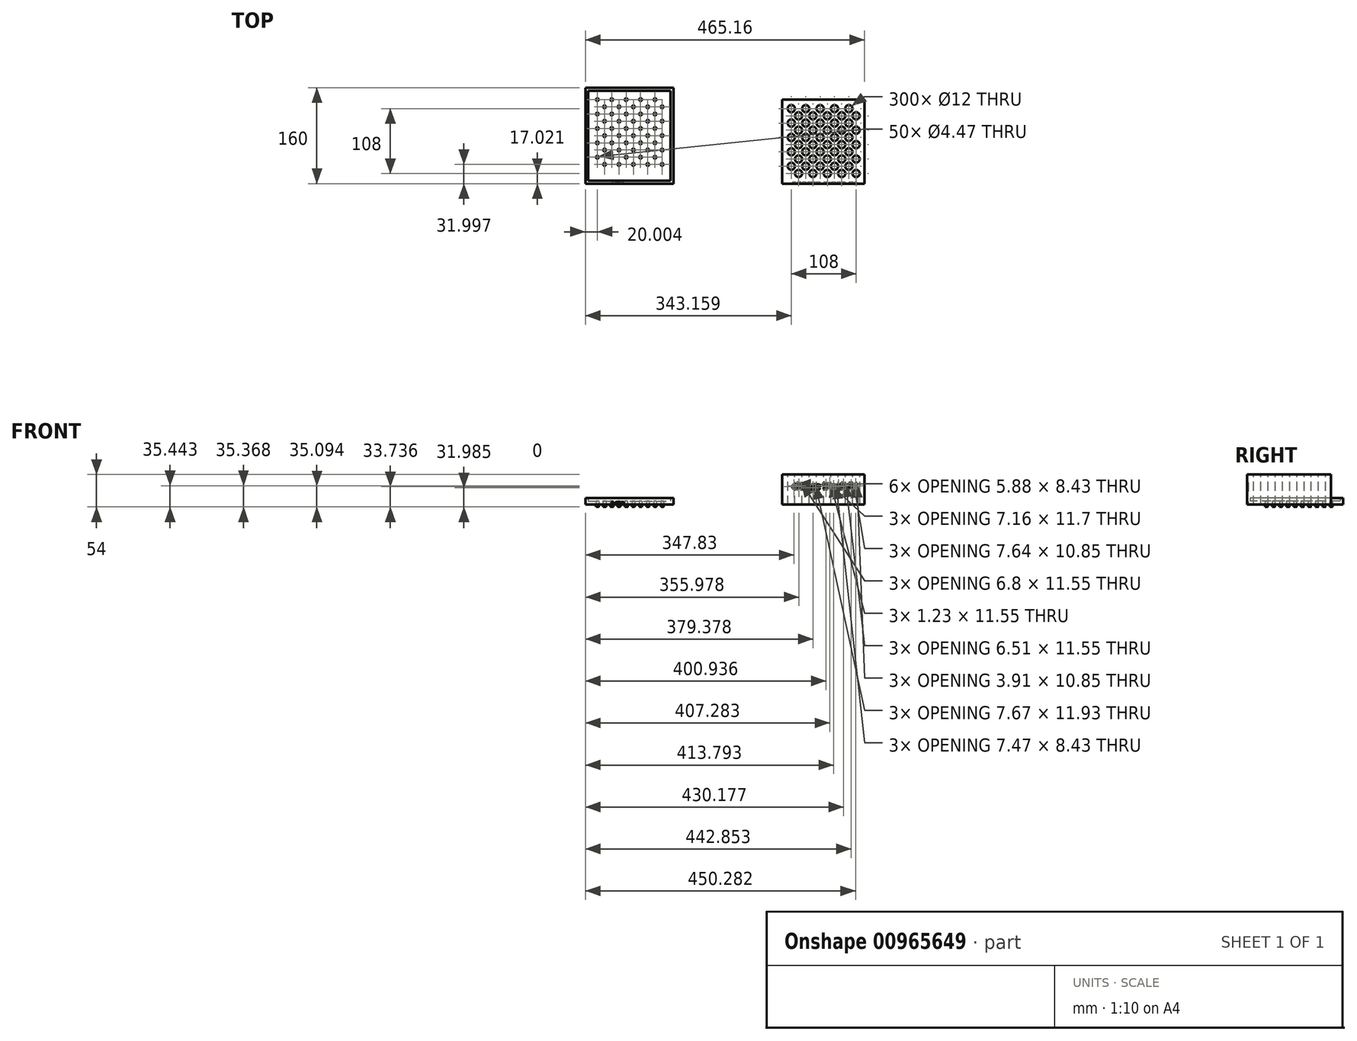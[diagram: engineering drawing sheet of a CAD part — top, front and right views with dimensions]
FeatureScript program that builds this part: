
annotation { "Feature Type Name" : "Feature", "Feature Type Description" : "" }
export const myFeature = defineFeature(function(context is Context, id is Id, definition is map)
    precondition{}
    {
        {
            var Q0;
            Q0=qCreatedBy(makeId("Top.planeOp"),FACE);
            var sketch = newSketch(context, id + "F0", { "sketchPlane" : qUnion([Q0])});
            skLineSegment(sketch, "E0.bottom", {"start": v(-132.2, 107.86) * mm, "end": v(14.8, 107.86) * mm});
            skLineSegment(sketch, "E0.top", {"start": v(-132.2, -52.14) * mm, "end": v(14.8, -52.14) * mm});
            skLineSegment(sketch, "E0.left", {"start": v(-132.2, 107.86) * mm, "end": v(-132.2, -52.14) * mm});
            skLineSegment(sketch, "E0.right", {"start": v(14.8, 107.86) * mm, "end": v(14.8, -52.14) * mm});
            skSolve(sketch);
        }
        {
            var Q0;
            Q0=qSketchRegion(id+"F0",true);
            extrude(context, id + "F1", {"entities" : qUnion([Q0]), "depth" : 6 * mm, "offsetDistance" : 25 * mm});
        }
        {
            var Q0;
            Q0=makeQuery(id+"F1.opExtrude","CAP_FACE",FACE,{"disambiguationData":[OSD([sQuery(id+"F0.wireOp",EDGE,"E0.bottom"),sQuery(id+"F0.wireOp",EDGE,"E0.top"),sQuery(id+"F0.wireOp",EDGE,"E0.left"),sQuery(id+"F0.wireOp",EDGE,"E0.right")])],"isStart":false});
            var sketch = newSketch(context, id + "F2", { "sketchPlane" : qUnion([Q0])});
            skCircle(sketch, "E1", {"center": v(-112.2, 87.86) * mm, "radius": 4 * mm});
            skCircle(sketch, "E2", {"center": v(-100.2, 75.86) * mm, "radius": 4 * mm});
            skCircle(sketch, "E3.0.1.0", {"center": v(-112.2, 63.86) * mm, "radius": 4 * mm});
            skCircle(sketch, "E3.0.1.1", {"center": v(-100.2, 51.86) * mm, "radius": 4 * mm});
            skCircle(sketch, "E3.0.2.0", {"center": v(-112.2, 39.86) * mm, "radius": 4 * mm});
            skCircle(sketch, "E3.0.2.1", {"center": v(-100.2, 27.86) * mm, "radius": 4 * mm});
            skCircle(sketch, "E3.0.3.0", {"center": v(-112.2, 15.86) * mm, "radius": 4 * mm});
            skCircle(sketch, "E3.0.3.1", {"center": v(-100.2, 3.86) * mm, "radius": 4 * mm});
            skCircle(sketch, "E3.0.4.0", {"center": v(-112.2, -8.14) * mm, "radius": 4 * mm});
            skCircle(sketch, "E3.0.4.1", {"center": v(-100.2, -20.14) * mm, "radius": 4 * mm});
            skCircle(sketch, "E3.1.0.0", {"center": v(-88.2, 87.86) * mm, "radius": 4 * mm});
            skCircle(sketch, "E3.1.0.1", {"center": v(-76.2, 75.86) * mm, "radius": 4 * mm});
            skCircle(sketch, "E3.1.1.0", {"center": v(-88.2, 63.86) * mm, "radius": 4 * mm});
            skCircle(sketch, "E3.1.1.1", {"center": v(-76.2, 51.86) * mm, "radius": 4 * mm});
            skCircle(sketch, "E3.1.2.0", {"center": v(-88.2, 39.86) * mm, "radius": 4 * mm});
            skCircle(sketch, "E3.1.2.1", {"center": v(-76.2, 27.86) * mm, "radius": 4 * mm});
            skCircle(sketch, "E3.1.3.0", {"center": v(-88.2, 15.86) * mm, "radius": 4 * mm});
            skCircle(sketch, "E3.1.3.1", {"center": v(-76.2, 3.86) * mm, "radius": 4 * mm});
            skCircle(sketch, "E3.1.4.0", {"center": v(-88.2, -8.14) * mm, "radius": 4 * mm});
            skCircle(sketch, "E3.1.4.1", {"center": v(-76.2, -20.14) * mm, "radius": 4 * mm});
            skCircle(sketch, "E3.2.0.0", {"center": v(-64.2, 87.86) * mm, "radius": 4 * mm});
            skCircle(sketch, "E3.2.0.1", {"center": v(-52.2, 75.86) * mm, "radius": 4 * mm});
            skCircle(sketch, "E3.2.1.0", {"center": v(-64.2, 63.86) * mm, "radius": 4 * mm});
            skCircle(sketch, "E3.2.1.1", {"center": v(-52.2, 51.86) * mm, "radius": 4 * mm});
            skCircle(sketch, "E3.2.2.0", {"center": v(-64.2, 39.86) * mm, "radius": 4 * mm});
            skCircle(sketch, "E3.2.2.1", {"center": v(-52.2, 27.86) * mm, "radius": 4 * mm});
            skCircle(sketch, "E3.2.3.0", {"center": v(-64.2, 15.86) * mm, "radius": 4 * mm});
            skCircle(sketch, "E3.2.3.1", {"center": v(-52.2, 3.86) * mm, "radius": 4 * mm});
            skCircle(sketch, "E3.2.4.0", {"center": v(-64.2, -8.14) * mm, "radius": 4 * mm});
            skCircle(sketch, "E3.2.4.1", {"center": v(-52.2, -20.14) * mm, "radius": 4 * mm});
            skCircle(sketch, "E3.3.0.0", {"center": v(-40.2, 87.86) * mm, "radius": 4 * mm});
            skCircle(sketch, "E3.3.0.1", {"center": v(-28.2, 75.86) * mm, "radius": 4 * mm});
            skCircle(sketch, "E3.3.1.0", {"center": v(-40.2, 63.86) * mm, "radius": 4 * mm});
            skCircle(sketch, "E3.3.1.1", {"center": v(-28.2, 51.86) * mm, "radius": 4 * mm});
            skCircle(sketch, "E3.3.2.0", {"center": v(-40.2, 39.86) * mm, "radius": 4 * mm});
            skCircle(sketch, "E3.3.2.1", {"center": v(-28.2, 27.86) * mm, "radius": 4 * mm});
            skCircle(sketch, "E3.3.3.0", {"center": v(-40.2, 15.86) * mm, "radius": 4 * mm});
            skCircle(sketch, "E3.3.3.1", {"center": v(-28.2, 3.86) * mm, "radius": 4 * mm});
            skCircle(sketch, "E3.3.4.0", {"center": v(-40.2, -8.14) * mm, "radius": 4 * mm});
            skCircle(sketch, "E3.3.4.1", {"center": v(-28.2, -20.14) * mm, "radius": 4 * mm});
            skCircle(sketch, "E3.4.0.0", {"center": v(-16.2, 87.86) * mm, "radius": 4 * mm});
            skCircle(sketch, "E3.4.0.1", {"center": v(-4.2, 75.86) * mm, "radius": 4 * mm});
            skCircle(sketch, "E3.4.1.0", {"center": v(-16.2, 63.86) * mm, "radius": 4 * mm});
            skCircle(sketch, "E3.4.1.1", {"center": v(-4.2, 51.86) * mm, "radius": 4 * mm});
            skCircle(sketch, "E3.4.2.0", {"center": v(-16.2, 39.86) * mm, "radius": 4 * mm});
            skCircle(sketch, "E3.4.2.1", {"center": v(-4.2, 27.86) * mm, "radius": 4 * mm});
            skCircle(sketch, "E3.4.3.0", {"center": v(-16.2, 15.86) * mm, "radius": 4 * mm});
            skCircle(sketch, "E3.4.3.1", {"center": v(-4.2, 3.86) * mm, "radius": 4 * mm});
            skCircle(sketch, "E3.4.4.0", {"center": v(-16.2, -8.14) * mm, "radius": 4 * mm});
            skCircle(sketch, "E3.4.4.1", {"center": v(-4.2, -20.14) * mm, "radius": 4 * mm});
            skLineSegment(sketch, "E3.direction1", {"start": v(-112.2, 87.86) * mm, "end": v(-88.2, 87.86) * mm, "construction": true});
            skLineSegment(sketch, "E3.direction2", {"start": v(-112.2, 87.86) * mm, "end": v(-112.2, 63.86) * mm, "construction": true});
            skSolve(sketch);
        }
        {
            var Q0;
            Q0=makeQuery(id+"F2.imprint","IMPRINT",FACE,{"disambiguationData":[TD([[makeQuery(id+"F2.imprint","IMPRINT",EDGE,{"derivedFrom":sQuery(id+"F2.wireOp",EDGE,"E3.0.1.0")}),1.0]])]});
            var Q1;
            Q1=makeQuery(id+"F2.imprint","IMPRINT",FACE,{"disambiguationData":[TD([[makeQuery(id+"F2.imprint","IMPRINT",EDGE,{"derivedFrom":sQuery(id+"F2.wireOp",EDGE,"E3.1.2.1")}),1.0]])]});
            var Q2;
            Q2=makeQuery(id+"F2.imprint","IMPRINT",FACE,{"disambiguationData":[TD([[makeQuery(id+"F2.imprint","IMPRINT",EDGE,{"derivedFrom":sQuery(id+"F2.wireOp",EDGE,"E3.1.3.0")}),1.0]])]});
            var Q3;
            Q3=makeQuery(id+"F2.imprint","IMPRINT",FACE,{"disambiguationData":[TD([[makeQuery(id+"F2.imprint","IMPRINT",EDGE,{"derivedFrom":sQuery(id+"F2.wireOp",EDGE,"E3.1.4.0")}),1.0]])]});
            var Q4;
            Q4=makeQuery(id+"F2.imprint","IMPRINT",FACE,{"disambiguationData":[TD([[makeQuery(id+"F2.imprint","IMPRINT",EDGE,{"derivedFrom":sQuery(id+"F2.wireOp",EDGE,"E3.2.4.1")}),1.0]])]});
            var Q5;
            Q5=makeQuery(id+"F2.imprint","IMPRINT",FACE,{"disambiguationData":[TD([[makeQuery(id+"F2.imprint","IMPRINT",EDGE,{"derivedFrom":sQuery(id+"F2.wireOp",EDGE,"E3.1.3.1")}),1.0]])]});
            var Q6;
            Q6=makeQuery(id+"F2.imprint","IMPRINT",FACE,{"disambiguationData":[TD([[makeQuery(id+"F2.imprint","IMPRINT",EDGE,{"derivedFrom":sQuery(id+"F2.wireOp",EDGE,"E3.3.0.0")}),1.0]])]});
            var Q7;
            Q7=makeQuery(id+"F2.imprint","IMPRINT",FACE,{"disambiguationData":[TD([[makeQuery(id+"F2.imprint","IMPRINT",EDGE,{"derivedFrom":sQuery(id+"F2.wireOp",EDGE,"E3.3.0.1")}),1.0]])]});
            var Q8;
            Q8=makeQuery(id+"F2.imprint","IMPRINT",FACE,{"disambiguationData":[TD([[makeQuery(id+"F2.imprint","IMPRINT",EDGE,{"derivedFrom":sQuery(id+"F2.wireOp",EDGE,"E3.3.1.0")}),1.0]])]});
            var Q9;
            Q9=makeQuery(id+"F2.imprint","IMPRINT",FACE,{"disambiguationData":[TD([[makeQuery(id+"F2.imprint","IMPRINT",EDGE,{"derivedFrom":sQuery(id+"F2.wireOp",EDGE,"E3.3.1.1")}),1.0]])]});
            var Q10;
            Q10=makeQuery(id+"F2.imprint","IMPRINT",FACE,{"disambiguationData":[TD([[makeQuery(id+"F2.imprint","IMPRINT",EDGE,{"derivedFrom":sQuery(id+"F2.wireOp",EDGE,"E3.3.2.0")}),1.0]])]});
            var Q11;
            Q11=makeQuery(id+"F2.imprint","IMPRINT",FACE,{"disambiguationData":[TD([[makeQuery(id+"F2.imprint","IMPRINT",EDGE,{"derivedFrom":sQuery(id+"F2.wireOp",EDGE,"E3.3.2.1")}),1.0]])]});
            var Q12;
            Q12=makeQuery(id+"F2.imprint","IMPRINT",FACE,{"disambiguationData":[TD([[makeQuery(id+"F2.imprint","IMPRINT",EDGE,{"derivedFrom":sQuery(id+"F2.wireOp",EDGE,"E3.3.3.0")}),1.0]])]});
            var Q13;
            Q13=makeQuery(id+"F2.imprint","IMPRINT",FACE,{"disambiguationData":[TD([[makeQuery(id+"F2.imprint","IMPRINT",EDGE,{"derivedFrom":sQuery(id+"F2.wireOp",EDGE,"E3.3.3.1")}),1.0]])]});
            var Q14;
            Q14=makeQuery(id+"F2.imprint","IMPRINT",FACE,{"disambiguationData":[TD([[makeQuery(id+"F2.imprint","IMPRINT",EDGE,{"derivedFrom":sQuery(id+"F2.wireOp",EDGE,"E3.3.4.0")}),1.0]])]});
            var Q15;
            Q15=makeQuery(id+"F2.imprint","IMPRINT",FACE,{"disambiguationData":[TD([[makeQuery(id+"F2.imprint","IMPRINT",EDGE,{"derivedFrom":sQuery(id+"F2.wireOp",EDGE,"E3.3.4.1")}),1.0]])]});
            var Q16;
            Q16=makeQuery(id+"F2.imprint","IMPRINT",FACE,{"disambiguationData":[TD([[makeQuery(id+"F2.imprint","IMPRINT",EDGE,{"derivedFrom":sQuery(id+"F2.wireOp",EDGE,"E3.4.0.0")}),1.0]])]});
            var Q17;
            Q17=makeQuery(id+"F2.imprint","IMPRINT",FACE,{"disambiguationData":[TD([[makeQuery(id+"F2.imprint","IMPRINT",EDGE,{"derivedFrom":sQuery(id+"F2.wireOp",EDGE,"E3.4.3.1")}),1.0]])]});
            var Q18;
            Q18=makeQuery(id+"F2.imprint","IMPRINT",FACE,{"disambiguationData":[TD([[makeQuery(id+"F2.imprint","IMPRINT",EDGE,{"derivedFrom":sQuery(id+"F2.wireOp",EDGE,"E1")}),1.0]])]});
            var Q19;
            Q19=makeQuery(id+"F2.imprint","IMPRINT",FACE,{"disambiguationData":[TD([[makeQuery(id+"F2.imprint","IMPRINT",EDGE,{"derivedFrom":sQuery(id+"F2.wireOp",EDGE,"E3.4.4.0")}),1.0]])]});
            var Q20;
            Q20=makeQuery(id+"F2.imprint","IMPRINT",FACE,{"disambiguationData":[TD([[makeQuery(id+"F2.imprint","IMPRINT",EDGE,{"derivedFrom":sQuery(id+"F2.wireOp",EDGE,"E2")}),1.0]])]});
            var Q21;
            Q21=makeQuery(id+"F2.imprint","IMPRINT",FACE,{"disambiguationData":[TD([[makeQuery(id+"F2.imprint","IMPRINT",EDGE,{"derivedFrom":sQuery(id+"F2.wireOp",EDGE,"E3.4.4.1")}),1.0]])]});
            var Q22;
            Q22=makeQuery(id+"F2.imprint","IMPRINT",FACE,{"disambiguationData":[TD([[makeQuery(id+"F2.imprint","IMPRINT",EDGE,{"derivedFrom":sQuery(id+"F2.wireOp",EDGE,"E3.0.1.1")}),1.0]])]});
            var Q23;
            Q23=makeQuery(id+"F2.imprint","IMPRINT",FACE,{"disambiguationData":[TD([[makeQuery(id+"F2.imprint","IMPRINT",EDGE,{"derivedFrom":sQuery(id+"F2.wireOp",EDGE,"E3.4.3.0")}),1.0]])]});
            var Q24;
            Q24=makeQuery(id+"F2.imprint","IMPRINT",FACE,{"disambiguationData":[TD([[makeQuery(id+"F2.imprint","IMPRINT",EDGE,{"derivedFrom":sQuery(id+"F2.wireOp",EDGE,"E3.4.2.1")}),1.0]])]});
            var Q25;
            Q25=makeQuery(id+"F2.imprint","IMPRINT",FACE,{"disambiguationData":[TD([[makeQuery(id+"F2.imprint","IMPRINT",EDGE,{"derivedFrom":sQuery(id+"F2.wireOp",EDGE,"E3.4.2.0")}),1.0]])]});
            var Q26;
            Q26=makeQuery(id+"F2.imprint","IMPRINT",FACE,{"disambiguationData":[TD([[makeQuery(id+"F2.imprint","IMPRINT",EDGE,{"derivedFrom":sQuery(id+"F2.wireOp",EDGE,"E3.4.1.1")}),1.0]])]});
            var Q27;
            Q27=makeQuery(id+"F2.imprint","IMPRINT",FACE,{"disambiguationData":[TD([[makeQuery(id+"F2.imprint","IMPRINT",EDGE,{"derivedFrom":sQuery(id+"F2.wireOp",EDGE,"E3.4.1.0")}),1.0]])]});
            var Q28;
            Q28=makeQuery(id+"F2.imprint","IMPRINT",FACE,{"disambiguationData":[TD([[makeQuery(id+"F2.imprint","IMPRINT",EDGE,{"derivedFrom":sQuery(id+"F2.wireOp",EDGE,"E3.4.0.1")}),1.0]])]});
            var Q29;
            Q29=makeQuery(id+"F2.imprint","IMPRINT",FACE,{"disambiguationData":[TD([[makeQuery(id+"F2.imprint","IMPRINT",EDGE,{"derivedFrom":sQuery(id+"F2.wireOp",EDGE,"E3.2.4.0")}),1.0]])]});
            var Q30;
            Q30=makeQuery(id+"F2.imprint","IMPRINT",FACE,{"disambiguationData":[TD([[makeQuery(id+"F2.imprint","IMPRINT",EDGE,{"derivedFrom":sQuery(id+"F2.wireOp",EDGE,"E3.2.3.1")}),1.0]])]});
            var Q31;
            Q31=makeQuery(id+"F2.imprint","IMPRINT",FACE,{"disambiguationData":[TD([[makeQuery(id+"F2.imprint","IMPRINT",EDGE,{"derivedFrom":sQuery(id+"F2.wireOp",EDGE,"E3.2.3.0")}),1.0]])]});
            var Q32;
            Q32=makeQuery(id+"F2.imprint","IMPRINT",FACE,{"disambiguationData":[TD([[makeQuery(id+"F2.imprint","IMPRINT",EDGE,{"derivedFrom":sQuery(id+"F2.wireOp",EDGE,"E3.2.2.1")}),1.0]])]});
            var Q33;
            Q33=makeQuery(id+"F2.imprint","IMPRINT",FACE,{"disambiguationData":[TD([[makeQuery(id+"F2.imprint","IMPRINT",EDGE,{"derivedFrom":sQuery(id+"F2.wireOp",EDGE,"E3.2.2.0")}),1.0]])]});
            var Q34;
            Q34=makeQuery(id+"F2.imprint","IMPRINT",FACE,{"disambiguationData":[TD([[makeQuery(id+"F2.imprint","IMPRINT",EDGE,{"derivedFrom":sQuery(id+"F2.wireOp",EDGE,"E3.2.1.1")}),1.0]])]});
            var Q35;
            Q35=makeQuery(id+"F2.imprint","IMPRINT",FACE,{"disambiguationData":[TD([[makeQuery(id+"F2.imprint","IMPRINT",EDGE,{"derivedFrom":sQuery(id+"F2.wireOp",EDGE,"E3.2.1.0")}),1.0]])]});
            var Q36;
            Q36=makeQuery(id+"F2.imprint","IMPRINT",FACE,{"disambiguationData":[TD([[makeQuery(id+"F2.imprint","IMPRINT",EDGE,{"derivedFrom":sQuery(id+"F2.wireOp",EDGE,"E3.2.0.1")}),1.0]])]});
            var Q37;
            Q37=makeQuery(id+"F2.imprint","IMPRINT",FACE,{"disambiguationData":[TD([[makeQuery(id+"F2.imprint","IMPRINT",EDGE,{"derivedFrom":sQuery(id+"F2.wireOp",EDGE,"E3.2.0.0")}),1.0]])]});
            var Q38;
            Q38=makeQuery(id+"F2.imprint","IMPRINT",FACE,{"disambiguationData":[TD([[makeQuery(id+"F2.imprint","IMPRINT",EDGE,{"derivedFrom":sQuery(id+"F2.wireOp",EDGE,"E3.1.4.1")}),1.0]])]});
            var Q39;
            Q39=makeQuery(id+"F2.imprint","IMPRINT",FACE,{"disambiguationData":[TD([[makeQuery(id+"F2.imprint","IMPRINT",EDGE,{"derivedFrom":sQuery(id+"F2.wireOp",EDGE,"E3.1.2.0")}),1.0]])]});
            var Q40;
            Q40=makeQuery(id+"F2.imprint","IMPRINT",FACE,{"disambiguationData":[TD([[makeQuery(id+"F2.imprint","IMPRINT",EDGE,{"derivedFrom":sQuery(id+"F2.wireOp",EDGE,"E3.1.1.1")}),1.0]])]});
            var Q41;
            Q41=makeQuery(id+"F2.imprint","IMPRINT",FACE,{"disambiguationData":[TD([[makeQuery(id+"F2.imprint","IMPRINT",EDGE,{"derivedFrom":sQuery(id+"F2.wireOp",EDGE,"E3.1.1.0")}),1.0]])]});
            var Q42;
            Q42=makeQuery(id+"F2.imprint","IMPRINT",FACE,{"disambiguationData":[TD([[makeQuery(id+"F2.imprint","IMPRINT",EDGE,{"derivedFrom":sQuery(id+"F2.wireOp",EDGE,"E3.1.0.1")}),1.0]])]});
            var Q43;
            Q43=makeQuery(id+"F2.imprint","IMPRINT",FACE,{"disambiguationData":[TD([[makeQuery(id+"F2.imprint","IMPRINT",EDGE,{"derivedFrom":sQuery(id+"F2.wireOp",EDGE,"E3.1.0.0")}),1.0]])]});
            var Q44;
            Q44=makeQuery(id+"F2.imprint","IMPRINT",FACE,{"disambiguationData":[TD([[makeQuery(id+"F2.imprint","IMPRINT",EDGE,{"derivedFrom":sQuery(id+"F2.wireOp",EDGE,"E3.0.4.1")}),1.0]])]});
            var Q45;
            Q45=makeQuery(id+"F2.imprint","IMPRINT",FACE,{"disambiguationData":[TD([[makeQuery(id+"F2.imprint","IMPRINT",EDGE,{"derivedFrom":sQuery(id+"F2.wireOp",EDGE,"E3.0.4.0")}),1.0]])]});
            var Q46;
            Q46=makeQuery(id+"F2.imprint","IMPRINT",FACE,{"disambiguationData":[TD([[makeQuery(id+"F2.imprint","IMPRINT",EDGE,{"derivedFrom":sQuery(id+"F2.wireOp",EDGE,"E3.0.3.1")}),1.0]])]});
            var Q47;
            Q47=makeQuery(id+"F2.imprint","IMPRINT",FACE,{"disambiguationData":[TD([[makeQuery(id+"F2.imprint","IMPRINT",EDGE,{"derivedFrom":sQuery(id+"F2.wireOp",EDGE,"E3.0.3.0")}),1.0]])]});
            var Q48;
            Q48=makeQuery(id+"F2.imprint","IMPRINT",FACE,{"disambiguationData":[TD([[makeQuery(id+"F2.imprint","IMPRINT",EDGE,{"derivedFrom":sQuery(id+"F2.wireOp",EDGE,"E3.0.2.1")}),1.0]])]});
            var Q49;
            Q49=makeQuery(id+"F2.imprint","IMPRINT",FACE,{"disambiguationData":[TD([[makeQuery(id+"F2.imprint","IMPRINT",EDGE,{"derivedFrom":sQuery(id+"F2.wireOp",EDGE,"E3.0.2.0")}),1.0]])]});
            extrude(context, id + "F3", {"entities" : qUnion([Q0, Q1, Q2, Q3, Q4, Q5, Q6, Q7, Q8, Q9, Q10, Q11, Q12, Q13, Q14, Q15, Q16, Q17, Q18, Q19, Q20, Q21, Q22, Q23, Q24, Q25, Q26, Q27, Q28, Q29, Q30, Q31, Q32, Q33, Q34, Q35, Q36, Q37, Q38, Q39, Q40, Q41, Q42, Q43, Q44, Q45, Q46, Q47, Q48, Q49]), "operationType" : NewBodyOperationType.ADD, "oppositeDirection" : true, "depth" : 10 * mm, "offsetDistance" : 25 * mm, "hasDraft" : true, "draftAngle" : 10 * degree, "draftPullDirection" : true});
        }
        {
            var Q0;
            Q0=makeQuery(id+"F1.opExtrude","CAP_FACE",FACE,{"disambiguationData":[OSD([sQuery(id+"F0.wireOp",EDGE,"E0.bottom"),sQuery(id+"F0.wireOp",EDGE,"E0.top"),sQuery(id+"F0.wireOp",EDGE,"E0.left"),sQuery(id+"F0.wireOp",EDGE,"E0.right")])],"isStart":false});
            var sketch = newSketch(context, id + "F4", { "sketchPlane" : qUnion([Q0])});
            skCircle(sketch, "E4", {"center": v(-112.2, 87.86) * mm, "radius": 1.75 * mm});
            skCircle(sketch, "E5", {"center": v(-100.2, 75.86) * mm, "radius": 1.75 * mm});
            skCircle(sketch, "E6.0.1.0", {"center": v(-112.2, 63.86) * mm, "radius": 1.75 * mm});
            skCircle(sketch, "E6.0.1.1", {"center": v(-100.2, 51.86) * mm, "radius": 1.75 * mm});
            skCircle(sketch, "E6.0.2.0", {"center": v(-112.2, 39.86) * mm, "radius": 1.75 * mm});
            skCircle(sketch, "E6.0.2.1", {"center": v(-100.2, 27.86) * mm, "radius": 1.75 * mm});
            skCircle(sketch, "E6.0.3.0", {"center": v(-112.2, 15.86) * mm, "radius": 1.75 * mm});
            skCircle(sketch, "E6.0.3.1", {"center": v(-100.2, 3.86) * mm, "radius": 1.75 * mm});
            skCircle(sketch, "E6.0.4.0", {"center": v(-112.2, -8.14) * mm, "radius": 1.75 * mm});
            skCircle(sketch, "E6.0.4.1", {"center": v(-100.2, -20.14) * mm, "radius": 1.75 * mm});
            skCircle(sketch, "E6.1.0.0", {"center": v(-88.2, 87.86) * mm, "radius": 1.75 * mm});
            skCircle(sketch, "E6.1.0.1", {"center": v(-76.2, 75.86) * mm, "radius": 1.75 * mm});
            skCircle(sketch, "E6.1.1.0", {"center": v(-88.2, 63.86) * mm, "radius": 1.75 * mm});
            skCircle(sketch, "E6.1.1.1", {"center": v(-76.2, 51.86) * mm, "radius": 1.75 * mm});
            skCircle(sketch, "E6.1.2.0", {"center": v(-88.2, 39.86) * mm, "radius": 1.75 * mm});
            skCircle(sketch, "E6.1.2.1", {"center": v(-76.2, 27.86) * mm, "radius": 1.75 * mm});
            skCircle(sketch, "E6.1.3.0", {"center": v(-88.2, 15.86) * mm, "radius": 1.75 * mm});
            skCircle(sketch, "E6.1.3.1", {"center": v(-76.2, 3.86) * mm, "radius": 1.75 * mm});
            skCircle(sketch, "E6.1.4.0", {"center": v(-88.2, -8.14) * mm, "radius": 1.75 * mm});
            skCircle(sketch, "E6.1.4.1", {"center": v(-76.2, -20.14) * mm, "radius": 1.75 * mm});
            skCircle(sketch, "E6.2.0.0", {"center": v(-64.2, 87.86) * mm, "radius": 1.75 * mm});
            skCircle(sketch, "E6.2.0.1", {"center": v(-52.2, 75.86) * mm, "radius": 1.75 * mm});
            skCircle(sketch, "E6.2.1.0", {"center": v(-64.2, 63.86) * mm, "radius": 1.75 * mm});
            skCircle(sketch, "E6.2.1.1", {"center": v(-52.2, 51.86) * mm, "radius": 1.75 * mm});
            skCircle(sketch, "E6.2.2.0", {"center": v(-64.2, 39.86) * mm, "radius": 1.75 * mm});
            skCircle(sketch, "E6.2.2.1", {"center": v(-52.2, 27.86) * mm, "radius": 1.75 * mm});
            skCircle(sketch, "E6.2.3.0", {"center": v(-64.2, 15.86) * mm, "radius": 1.75 * mm});
            skCircle(sketch, "E6.2.3.1", {"center": v(-52.2, 3.86) * mm, "radius": 1.75 * mm});
            skCircle(sketch, "E6.2.4.0", {"center": v(-64.2, -8.14) * mm, "radius": 1.75 * mm});
            skCircle(sketch, "E6.2.4.1", {"center": v(-52.2, -20.14) * mm, "radius": 1.75 * mm});
            skCircle(sketch, "E6.3.0.0", {"center": v(-40.2, 87.86) * mm, "radius": 1.75 * mm});
            skCircle(sketch, "E6.3.0.1", {"center": v(-28.2, 75.86) * mm, "radius": 1.75 * mm});
            skCircle(sketch, "E6.3.1.0", {"center": v(-40.2, 63.86) * mm, "radius": 1.75 * mm});
            skCircle(sketch, "E6.3.1.1", {"center": v(-28.2, 51.86) * mm, "radius": 1.75 * mm});
            skCircle(sketch, "E6.3.2.0", {"center": v(-40.2, 39.86) * mm, "radius": 1.75 * mm});
            skCircle(sketch, "E6.3.2.1", {"center": v(-28.2, 27.86) * mm, "radius": 1.75 * mm});
            skCircle(sketch, "E6.3.3.0", {"center": v(-40.2, 15.86) * mm, "radius": 1.75 * mm});
            skCircle(sketch, "E6.3.3.1", {"center": v(-28.2, 3.86) * mm, "radius": 1.75 * mm});
            skCircle(sketch, "E6.3.4.0", {"center": v(-40.2, -8.14) * mm, "radius": 1.75 * mm});
            skCircle(sketch, "E6.3.4.1", {"center": v(-28.2, -20.14) * mm, "radius": 1.75 * mm});
            skCircle(sketch, "E6.4.0.0", {"center": v(-16.2, 87.86) * mm, "radius": 1.75 * mm});
            skCircle(sketch, "E6.4.0.1", {"center": v(-4.2, 75.86) * mm, "radius": 1.75 * mm});
            skCircle(sketch, "E6.4.1.0", {"center": v(-16.2, 63.86) * mm, "radius": 1.75 * mm});
            skCircle(sketch, "E6.4.1.1", {"center": v(-4.2, 51.86) * mm, "radius": 1.75 * mm});
            skCircle(sketch, "E6.4.2.0", {"center": v(-16.2, 39.86) * mm, "radius": 1.75 * mm});
            skCircle(sketch, "E6.4.2.1", {"center": v(-4.2, 27.86) * mm, "radius": 1.75 * mm});
            skCircle(sketch, "E6.4.3.0", {"center": v(-16.2, 15.86) * mm, "radius": 1.75 * mm});
            skCircle(sketch, "E6.4.3.1", {"center": v(-4.2, 3.86) * mm, "radius": 1.75 * mm});
            skCircle(sketch, "E6.4.4.0", {"center": v(-16.2, -8.14) * mm, "radius": 1.75 * mm});
            skCircle(sketch, "E6.4.4.1", {"center": v(-4.2, -20.14) * mm, "radius": 1.75 * mm});
            skLineSegment(sketch, "E6.direction1", {"start": v(-112.2, 87.86) * mm, "end": v(-88.2, 87.86) * mm, "construction": true});
            skLineSegment(sketch, "E6.direction2", {"start": v(-112.2, 87.86) * mm, "end": v(-112.2, 63.86) * mm, "construction": true});
            skSolve(sketch);
        }
        {
            var Q0;
            Q0=makeQuery(id+"F3.opExtrude","CAP_FACE",FACE,{"disambiguationData":[OSD([sQuery(id+"F2.wireOp",EDGE,"E3.1.4.1")])],"isStart":false});
            var Q1;
            Q1=makeQuery(id+"F3.opExtrude","CAP_FACE",FACE,{"disambiguationData":[OSD([sQuery(id+"F2.wireOp",EDGE,"E3.4.0.1")])],"isStart":false});
            var Q2;
            Q2=makeQuery(id+"F3.opExtrude","CAP_FACE",FACE,{"disambiguationData":[OSD([sQuery(id+"F2.wireOp",EDGE,"E3.3.0.0")])],"isStart":false});
            var Q3;
            Q3=makeQuery(id+"F3.opExtrude","CAP_FACE",FACE,{"disambiguationData":[OSD([sQuery(id+"F2.wireOp",EDGE,"E3.1.4.0")])],"isStart":false});
            var Q4;
            Q4=makeQuery(id+"F3.opExtrude","CAP_FACE",FACE,{"disambiguationData":[OSD([sQuery(id+"F2.wireOp",EDGE,"E3.2.1.1")])],"isStart":false});
            var Q5;
            Q5=makeQuery(id+"F3.opExtrude","CAP_FACE",FACE,{"disambiguationData":[OSD([sQuery(id+"F2.wireOp",EDGE,"E3.2.0.0")])],"isStart":false});
            var Q6;
            Q6=makeQuery(id+"F3.opExtrude","CAP_FACE",FACE,{"disambiguationData":[OSD([sQuery(id+"F2.wireOp",EDGE,"E3.0.3.1")])],"isStart":false});
            var Q7;
            Q7=makeQuery(id+"F3.opExtrude","CAP_FACE",FACE,{"disambiguationData":[OSD([sQuery(id+"F2.wireOp",EDGE,"E3.4.0.0")])],"isStart":false});
            var Q8;
            Q8=makeQuery(id+"F3.opExtrude","CAP_FACE",FACE,{"disambiguationData":[OSD([sQuery(id+"F2.wireOp",EDGE,"E3.4.4.1")])],"isStart":false});
            var Q9;
            Q9=makeQuery(id+"F3.opExtrude","CAP_FACE",FACE,{"disambiguationData":[OSD([sQuery(id+"F2.wireOp",EDGE,"E3.3.3.0")])],"isStart":false});
            var Q10;
            Q10=makeQuery(id+"F3.opExtrude","CAP_FACE",FACE,{"disambiguationData":[OSD([sQuery(id+"F2.wireOp",EDGE,"E3.0.1.0")])],"isStart":false});
            var Q11;
            Q11=makeQuery(id+"F3.opExtrude","CAP_FACE",FACE,{"disambiguationData":[OSD([sQuery(id+"F2.wireOp",EDGE,"E3.1.2.1")])],"isStart":false});
            var Q12;
            Q12=makeQuery(id+"F3.opExtrude","CAP_FACE",FACE,{"disambiguationData":[OSD([sQuery(id+"F2.wireOp",EDGE,"E3.3.0.1")])],"isStart":false});
            var Q13;
            Q13=makeQuery(id+"F3.opExtrude","CAP_FACE",FACE,{"disambiguationData":[OSD([sQuery(id+"F2.wireOp",EDGE,"E3.2.2.1")])],"isStart":false});
            var Q14;
            Q14=makeQuery(id+"F3.opExtrude","CAP_FACE",FACE,{"disambiguationData":[OSD([sQuery(id+"F2.wireOp",EDGE,"E3.1.1.1")])],"isStart":false});
            var Q15;
            Q15=makeQuery(id+"F3.opExtrude","CAP_FACE",FACE,{"disambiguationData":[OSD([sQuery(id+"F2.wireOp",EDGE,"E3.2.2.0")])],"isStart":false});
            var Q16;
            Q16=makeQuery(id+"F3.opExtrude","CAP_FACE",FACE,{"disambiguationData":[OSD([sQuery(id+"F2.wireOp",EDGE,"E3.4.2.0")])],"isStart":false});
            var Q17;
            Q17=makeQuery(id+"F3.opExtrude","CAP_FACE",FACE,{"disambiguationData":[OSD([sQuery(id+"F2.wireOp",EDGE,"E3.4.2.1")])],"isStart":false});
            var Q18;
            Q18=makeQuery(id+"F3.opExtrude","CAP_FACE",FACE,{"disambiguationData":[OSD([sQuery(id+"F2.wireOp",EDGE,"E3.2.3.1")])],"isStart":false});
            var Q19;
            Q19=makeQuery(id+"F3.opExtrude","CAP_FACE",FACE,{"disambiguationData":[OSD([sQuery(id+"F2.wireOp",EDGE,"E3.0.3.0")])],"isStart":false});
            var Q20;
            Q20=makeQuery(id+"F3.opExtrude","CAP_FACE",FACE,{"disambiguationData":[OSD([sQuery(id+"F2.wireOp",EDGE,"E3.3.4.1")])],"isStart":false});
            var Q21;
            Q21=makeQuery(id+"F3.opExtrude","CAP_FACE",FACE,{"disambiguationData":[OSD([sQuery(id+"F2.wireOp",EDGE,"E3.1.0.1")])],"isStart":false});
            var Q22;
            Q22=makeQuery(id+"F3.opExtrude","CAP_FACE",FACE,{"disambiguationData":[OSD([sQuery(id+"F2.wireOp",EDGE,"E3.2.0.1")])],"isStart":false});
            var Q23;
            Q23=makeQuery(id+"F3.opExtrude","CAP_FACE",FACE,{"disambiguationData":[OSD([sQuery(id+"F2.wireOp",EDGE,"E3.3.1.1")])],"isStart":false});
            var Q24;
            Q24=makeQuery(id+"F3.opExtrude","CAP_FACE",FACE,{"disambiguationData":[OSD([sQuery(id+"F2.wireOp",EDGE,"E3.0.4.0")])],"isStart":false});
            var Q25;
            Q25=makeQuery(id+"F3.opExtrude","CAP_FACE",FACE,{"disambiguationData":[OSD([sQuery(id+"F2.wireOp",EDGE,"E3.3.4.0")])],"isStart":false});
            var Q26;
            Q26=makeQuery(id+"F3.opExtrude","CAP_FACE",FACE,{"disambiguationData":[OSD([sQuery(id+"F2.wireOp",EDGE,"E3.1.0.0")])],"isStart":false});
            var Q27;
            Q27=makeQuery(id+"F3.opExtrude","CAP_FACE",FACE,{"disambiguationData":[OSD([sQuery(id+"F2.wireOp",EDGE,"E3.1.3.1")])],"isStart":false});
            var Q28;
            Q28=makeQuery(id+"F3.opExtrude","CAP_FACE",FACE,{"disambiguationData":[OSD([sQuery(id+"F2.wireOp",EDGE,"E1")])],"isStart":false});
            var Q29;
            Q29=makeQuery(id+"F3.opExtrude","CAP_FACE",FACE,{"disambiguationData":[OSD([sQuery(id+"F2.wireOp",EDGE,"E3.1.3.0")])],"isStart":false});
            var Q30;
            Q30=makeQuery(id+"F3.opExtrude","CAP_FACE",FACE,{"disambiguationData":[OSD([sQuery(id+"F2.wireOp",EDGE,"E3.3.3.1")])],"isStart":false});
            var Q31;
            Q31=makeQuery(id+"F3.opExtrude","CAP_FACE",FACE,{"disambiguationData":[OSD([sQuery(id+"F2.wireOp",EDGE,"E3.0.4.1")])],"isStart":false});
            var Q32;
            Q32=makeQuery(id+"F3.opExtrude","CAP_FACE",FACE,{"disambiguationData":[OSD([sQuery(id+"F2.wireOp",EDGE,"E3.1.1.0")])],"isStart":false});
            var Q33;
            Q33=makeQuery(id+"F3.opExtrude","CAP_FACE",FACE,{"disambiguationData":[OSD([sQuery(id+"F2.wireOp",EDGE,"E3.3.2.0")])],"isStart":false});
            var Q34;
            Q34=makeQuery(id+"F3.opExtrude","CAP_FACE",FACE,{"disambiguationData":[OSD([sQuery(id+"F2.wireOp",EDGE,"E3.4.3.0")])],"isStart":false});
            var Q35;
            Q35=makeQuery(id+"F3.opExtrude","CAP_FACE",FACE,{"disambiguationData":[OSD([sQuery(id+"F2.wireOp",EDGE,"E2")])],"isStart":false});
            var Q36;
            Q36=makeQuery(id+"F3.opExtrude","CAP_FACE",FACE,{"disambiguationData":[OSD([sQuery(id+"F2.wireOp",EDGE,"E3.2.4.1")])],"isStart":false});
            var Q37;
            Q37=makeQuery(id+"F3.opExtrude","CAP_FACE",FACE,{"disambiguationData":[OSD([sQuery(id+"F2.wireOp",EDGE,"E3.3.1.0")])],"isStart":false});
            var Q38;
            Q38=makeQuery(id+"F3.opExtrude","CAP_FACE",FACE,{"disambiguationData":[OSD([sQuery(id+"F2.wireOp",EDGE,"E3.2.4.0")])],"isStart":false});
            var Q39;
            Q39=makeQuery(id+"F3.opExtrude","CAP_FACE",FACE,{"disambiguationData":[OSD([sQuery(id+"F2.wireOp",EDGE,"E3.3.2.1")])],"isStart":false});
            var Q40;
            Q40=makeQuery(id+"F3.opExtrude","CAP_FACE",FACE,{"disambiguationData":[OSD([sQuery(id+"F2.wireOp",EDGE,"E3.0.1.1")])],"isStart":false});
            var Q41;
            Q41=makeQuery(id+"F3.opExtrude","CAP_FACE",FACE,{"disambiguationData":[OSD([sQuery(id+"F2.wireOp",EDGE,"E3.4.4.0")])],"isStart":false});
            var Q42;
            Q42=makeQuery(id+"F3.opExtrude","CAP_FACE",FACE,{"disambiguationData":[OSD([sQuery(id+"F2.wireOp",EDGE,"E3.0.2.1")])],"isStart":false});
            var Q43;
            Q43=makeQuery(id+"F3.opExtrude","CAP_FACE",FACE,{"disambiguationData":[OSD([sQuery(id+"F2.wireOp",EDGE,"E3.1.2.0")])],"isStart":false});
            var Q44;
            Q44=makeQuery(id+"F3.opExtrude","CAP_FACE",FACE,{"disambiguationData":[OSD([sQuery(id+"F2.wireOp",EDGE,"E3.4.1.1")])],"isStart":false});
            var Q45;
            Q45=makeQuery(id+"F3.opExtrude","CAP_FACE",FACE,{"disambiguationData":[OSD([sQuery(id+"F2.wireOp",EDGE,"E3.4.1.0")])],"isStart":false});
            var Q46;
            Q46=makeQuery(id+"F3.opExtrude","CAP_FACE",FACE,{"disambiguationData":[OSD([sQuery(id+"F2.wireOp",EDGE,"E3.4.3.1")])],"isStart":false});
            var Q47;
            Q47=makeQuery(id+"F3.opExtrude","CAP_FACE",FACE,{"disambiguationData":[OSD([sQuery(id+"F2.wireOp",EDGE,"E3.0.2.0")])],"isStart":false});
            var Q48;
            Q48=makeQuery(id+"F3.opExtrude","CAP_FACE",FACE,{"disambiguationData":[OSD([sQuery(id+"F2.wireOp",EDGE,"E3.2.3.0")])],"isStart":false});
            var Q49;
            Q49=makeQuery(id+"F3.opExtrude","CAP_FACE",FACE,{"disambiguationData":[OSD([sQuery(id+"F2.wireOp",EDGE,"E3.2.1.0")])],"isStart":false});
            var Q50;
            Q50=makeQuery(id+"F4.imprint","IMPRINT",FACE,{"disambiguationData":[TD([[makeQuery(id+"F4.imprint","IMPRINT",EDGE,{"derivedFrom":sQuery(id+"F4.wireOp",EDGE,"E6.4.4.0")}),1.0]])]});
            var Q51;
            Q51=makeQuery(id+"F4.imprint","IMPRINT",FACE,{"disambiguationData":[TD([[makeQuery(id+"F4.imprint","IMPRINT",EDGE,{"derivedFrom":sQuery(id+"F4.wireOp",EDGE,"E6.4.4.1")}),1.0]])]});
            var Q52;
            Q52=makeQuery(id+"F4.imprint","IMPRINT",FACE,{"disambiguationData":[TD([[makeQuery(id+"F4.imprint","IMPRINT",EDGE,{"derivedFrom":sQuery(id+"F4.wireOp",EDGE,"E6.2.2.0")}),1.0]])]});
            var Q53;
            Q53=makeQuery(id+"F4.imprint","IMPRINT",FACE,{"disambiguationData":[TD([[makeQuery(id+"F4.imprint","IMPRINT",EDGE,{"derivedFrom":sQuery(id+"F4.wireOp",EDGE,"E6.2.2.1")}),1.0]])]});
            var Q54;
            Q54=makeQuery(id+"F4.imprint","IMPRINT",FACE,{"disambiguationData":[TD([[makeQuery(id+"F4.imprint","IMPRINT",EDGE,{"derivedFrom":sQuery(id+"F4.wireOp",EDGE,"E6.4.3.1")}),1.0]])]});
            var Q55;
            Q55=makeQuery(id+"F4.imprint","IMPRINT",FACE,{"disambiguationData":[TD([[makeQuery(id+"F4.imprint","IMPRINT",EDGE,{"derivedFrom":sQuery(id+"F4.wireOp",EDGE,"E6.0.1.1")}),1.0]])]});
            var Q56;
            Q56=makeQuery(id+"F4.imprint","IMPRINT",FACE,{"disambiguationData":[TD([[makeQuery(id+"F4.imprint","IMPRINT",EDGE,{"derivedFrom":sQuery(id+"F4.wireOp",EDGE,"E6.0.2.0")}),1.0]])]});
            var Q57;
            Q57=makeQuery(id+"F4.imprint","IMPRINT",FACE,{"disambiguationData":[TD([[makeQuery(id+"F4.imprint","IMPRINT",EDGE,{"derivedFrom":sQuery(id+"F4.wireOp",EDGE,"E6.0.2.1")}),1.0]])]});
            var Q58;
            Q58=makeQuery(id+"F4.imprint","IMPRINT",FACE,{"disambiguationData":[TD([[makeQuery(id+"F4.imprint","IMPRINT",EDGE,{"derivedFrom":sQuery(id+"F4.wireOp",EDGE,"E6.0.3.0")}),1.0]])]});
            var Q59;
            Q59=makeQuery(id+"F4.imprint","IMPRINT",FACE,{"disambiguationData":[TD([[makeQuery(id+"F4.imprint","IMPRINT",EDGE,{"derivedFrom":sQuery(id+"F4.wireOp",EDGE,"E6.0.3.1")}),1.0]])]});
            var Q60;
            Q60=makeQuery(id+"F4.imprint","IMPRINT",FACE,{"disambiguationData":[TD([[makeQuery(id+"F4.imprint","IMPRINT",EDGE,{"derivedFrom":sQuery(id+"F4.wireOp",EDGE,"E6.0.4.0")}),1.0]])]});
            var Q61;
            Q61=makeQuery(id+"F4.imprint","IMPRINT",FACE,{"disambiguationData":[TD([[makeQuery(id+"F4.imprint","IMPRINT",EDGE,{"derivedFrom":sQuery(id+"F4.wireOp",EDGE,"E6.0.4.1")}),1.0]])]});
            var Q62;
            Q62=makeQuery(id+"F4.imprint","IMPRINT",FACE,{"disambiguationData":[TD([[makeQuery(id+"F4.imprint","IMPRINT",EDGE,{"derivedFrom":sQuery(id+"F4.wireOp",EDGE,"E6.1.0.1")}),1.0]])]});
            var Q63;
            Q63=makeQuery(id+"F4.imprint","IMPRINT",FACE,{"disambiguationData":[TD([[makeQuery(id+"F4.imprint","IMPRINT",EDGE,{"derivedFrom":sQuery(id+"F4.wireOp",EDGE,"E6.1.1.0")}),1.0]])]});
            var Q64;
            Q64=makeQuery(id+"F4.imprint","IMPRINT",FACE,{"disambiguationData":[TD([[makeQuery(id+"F4.imprint","IMPRINT",EDGE,{"derivedFrom":sQuery(id+"F4.wireOp",EDGE,"E6.1.1.1")}),1.0]])]});
            var Q65;
            Q65=makeQuery(id+"F4.imprint","IMPRINT",FACE,{"disambiguationData":[TD([[makeQuery(id+"F4.imprint","IMPRINT",EDGE,{"derivedFrom":sQuery(id+"F4.wireOp",EDGE,"E6.2.0.0")}),1.0]])]});
            var Q66;
            Q66=makeQuery(id+"F4.imprint","IMPRINT",FACE,{"disambiguationData":[TD([[makeQuery(id+"F4.imprint","IMPRINT",EDGE,{"derivedFrom":sQuery(id+"F4.wireOp",EDGE,"E6.2.0.1")}),1.0]])]});
            var Q67;
            Q67=makeQuery(id+"F4.imprint","IMPRINT",FACE,{"disambiguationData":[TD([[makeQuery(id+"F4.imprint","IMPRINT",EDGE,{"derivedFrom":sQuery(id+"F4.wireOp",EDGE,"E6.2.1.0")}),1.0]])]});
            var Q68;
            Q68=makeQuery(id+"F4.imprint","IMPRINT",FACE,{"disambiguationData":[TD([[makeQuery(id+"F4.imprint","IMPRINT",EDGE,{"derivedFrom":sQuery(id+"F4.wireOp",EDGE,"E6.2.1.1")}),1.0]])]});
            var Q69;
            Q69=makeQuery(id+"F4.imprint","IMPRINT",FACE,{"disambiguationData":[TD([[makeQuery(id+"F4.imprint","IMPRINT",EDGE,{"derivedFrom":sQuery(id+"F4.wireOp",EDGE,"E6.1.4.1")}),1.0]])]});
            var Q70;
            Q70=makeQuery(id+"F4.imprint","IMPRINT",FACE,{"disambiguationData":[TD([[makeQuery(id+"F4.imprint","IMPRINT",EDGE,{"derivedFrom":sQuery(id+"F4.wireOp",EDGE,"E6.1.4.0")}),1.0]])]});
            var Q71;
            Q71=makeQuery(id+"F4.imprint","IMPRINT",FACE,{"disambiguationData":[TD([[makeQuery(id+"F4.imprint","IMPRINT",EDGE,{"derivedFrom":sQuery(id+"F4.wireOp",EDGE,"E6.1.3.1")}),1.0]])]});
            var Q72;
            Q72=makeQuery(id+"F4.imprint","IMPRINT",FACE,{"disambiguationData":[TD([[makeQuery(id+"F4.imprint","IMPRINT",EDGE,{"derivedFrom":sQuery(id+"F4.wireOp",EDGE,"E6.1.3.0")}),1.0]])]});
            var Q73;
            Q73=makeQuery(id+"F4.imprint","IMPRINT",FACE,{"disambiguationData":[TD([[makeQuery(id+"F4.imprint","IMPRINT",EDGE,{"derivedFrom":sQuery(id+"F4.wireOp",EDGE,"E6.1.2.1")}),1.0]])]});
            var Q74;
            Q74=makeQuery(id+"F4.imprint","IMPRINT",FACE,{"disambiguationData":[TD([[makeQuery(id+"F4.imprint","IMPRINT",EDGE,{"derivedFrom":sQuery(id+"F4.wireOp",EDGE,"E6.1.2.0")}),1.0]])]});
            var Q75;
            Q75=makeQuery(id+"F4.imprint","IMPRINT",FACE,{"disambiguationData":[TD([[makeQuery(id+"F4.imprint","IMPRINT",EDGE,{"derivedFrom":sQuery(id+"F4.wireOp",EDGE,"E6.4.3.0")}),1.0]])]});
            var Q76;
            Q76=makeQuery(id+"F4.imprint","IMPRINT",FACE,{"disambiguationData":[TD([[makeQuery(id+"F4.imprint","IMPRINT",EDGE,{"derivedFrom":sQuery(id+"F4.wireOp",EDGE,"E6.4.2.1")}),1.0]])]});
            var Q77;
            Q77=makeQuery(id+"F4.imprint","IMPRINT",FACE,{"disambiguationData":[TD([[makeQuery(id+"F4.imprint","IMPRINT",EDGE,{"derivedFrom":sQuery(id+"F4.wireOp",EDGE,"E6.4.2.0")}),1.0]])]});
            var Q78;
            Q78=makeQuery(id+"F4.imprint","IMPRINT",FACE,{"disambiguationData":[TD([[makeQuery(id+"F4.imprint","IMPRINT",EDGE,{"derivedFrom":sQuery(id+"F4.wireOp",EDGE,"E6.4.1.1")}),1.0]])]});
            var Q79;
            Q79=makeQuery(id+"F4.imprint","IMPRINT",FACE,{"disambiguationData":[TD([[makeQuery(id+"F4.imprint","IMPRINT",EDGE,{"derivedFrom":sQuery(id+"F4.wireOp",EDGE,"E6.4.1.0")}),1.0]])]});
            var Q80;
            Q80=makeQuery(id+"F4.imprint","IMPRINT",FACE,{"disambiguationData":[TD([[makeQuery(id+"F4.imprint","IMPRINT",EDGE,{"derivedFrom":sQuery(id+"F4.wireOp",EDGE,"E6.4.0.1")}),1.0]])]});
            var Q81;
            Q81=makeQuery(id+"F4.imprint","IMPRINT",FACE,{"disambiguationData":[TD([[makeQuery(id+"F4.imprint","IMPRINT",EDGE,{"derivedFrom":sQuery(id+"F4.wireOp",EDGE,"E6.4.0.0")}),1.0]])]});
            var Q82;
            Q82=makeQuery(id+"F4.imprint","IMPRINT",FACE,{"disambiguationData":[TD([[makeQuery(id+"F4.imprint","IMPRINT",EDGE,{"derivedFrom":sQuery(id+"F4.wireOp",EDGE,"E6.3.4.1")}),1.0]])]});
            var Q83;
            Q83=makeQuery(id+"F4.imprint","IMPRINT",FACE,{"disambiguationData":[TD([[makeQuery(id+"F4.imprint","IMPRINT",EDGE,{"derivedFrom":sQuery(id+"F4.wireOp",EDGE,"E6.3.4.0")}),1.0]])]});
            var Q84;
            Q84=makeQuery(id+"F4.imprint","IMPRINT",FACE,{"disambiguationData":[TD([[makeQuery(id+"F4.imprint","IMPRINT",EDGE,{"derivedFrom":sQuery(id+"F4.wireOp",EDGE,"E6.3.3.1")}),1.0]])]});
            var Q85;
            Q85=makeQuery(id+"F4.imprint","IMPRINT",FACE,{"disambiguationData":[TD([[makeQuery(id+"F4.imprint","IMPRINT",EDGE,{"derivedFrom":sQuery(id+"F4.wireOp",EDGE,"E6.3.3.0")}),1.0]])]});
            var Q86;
            Q86=makeQuery(id+"F4.imprint","IMPRINT",FACE,{"disambiguationData":[TD([[makeQuery(id+"F4.imprint","IMPRINT",EDGE,{"derivedFrom":sQuery(id+"F4.wireOp",EDGE,"E6.3.2.1")}),1.0]])]});
            var Q87;
            Q87=makeQuery(id+"F4.imprint","IMPRINT",FACE,{"disambiguationData":[TD([[makeQuery(id+"F4.imprint","IMPRINT",EDGE,{"derivedFrom":sQuery(id+"F4.wireOp",EDGE,"E6.3.2.0")}),1.0]])]});
            var Q88;
            Q88=makeQuery(id+"F4.imprint","IMPRINT",FACE,{"disambiguationData":[TD([[makeQuery(id+"F4.imprint","IMPRINT",EDGE,{"derivedFrom":sQuery(id+"F4.wireOp",EDGE,"E6.3.1.1")}),1.0]])]});
            var Q89;
            Q89=makeQuery(id+"F4.imprint","IMPRINT",FACE,{"disambiguationData":[TD([[makeQuery(id+"F4.imprint","IMPRINT",EDGE,{"derivedFrom":sQuery(id+"F4.wireOp",EDGE,"E6.3.1.0")}),1.0]])]});
            var Q90;
            Q90=makeQuery(id+"F4.imprint","IMPRINT",FACE,{"disambiguationData":[TD([[makeQuery(id+"F4.imprint","IMPRINT",EDGE,{"derivedFrom":sQuery(id+"F4.wireOp",EDGE,"E6.3.0.1")}),1.0]])]});
            var Q91;
            Q91=makeQuery(id+"F4.imprint","IMPRINT",FACE,{"disambiguationData":[TD([[makeQuery(id+"F4.imprint","IMPRINT",EDGE,{"derivedFrom":sQuery(id+"F4.wireOp",EDGE,"E6.3.0.0")}),1.0]])]});
            var Q92;
            Q92=makeQuery(id+"F4.imprint","IMPRINT",FACE,{"disambiguationData":[TD([[makeQuery(id+"F4.imprint","IMPRINT",EDGE,{"derivedFrom":sQuery(id+"F4.wireOp",EDGE,"E6.0.1.0")}),1.0]])]});
            var Q93;
            Q93=makeQuery(id+"F4.imprint","IMPRINT",FACE,{"disambiguationData":[TD([[makeQuery(id+"F4.imprint","IMPRINT",EDGE,{"derivedFrom":sQuery(id+"F4.wireOp",EDGE,"E5")}),1.0]])]});
            var Q94;
            Q94=makeQuery(id+"F4.imprint","IMPRINT",FACE,{"disambiguationData":[TD([[makeQuery(id+"F4.imprint","IMPRINT",EDGE,{"derivedFrom":sQuery(id+"F4.wireOp",EDGE,"E6.2.4.1")}),1.0]])]});
            var Q95;
            Q95=makeQuery(id+"F4.imprint","IMPRINT",FACE,{"disambiguationData":[TD([[makeQuery(id+"F4.imprint","IMPRINT",EDGE,{"derivedFrom":sQuery(id+"F4.wireOp",EDGE,"E6.2.4.0")}),1.0]])]});
            var Q96;
            Q96=makeQuery(id+"F4.imprint","IMPRINT",FACE,{"disambiguationData":[TD([[makeQuery(id+"F4.imprint","IMPRINT",EDGE,{"derivedFrom":sQuery(id+"F4.wireOp",EDGE,"E6.2.3.1")}),1.0]])]});
            var Q97;
            Q97=makeQuery(id+"F4.imprint","IMPRINT",FACE,{"disambiguationData":[TD([[makeQuery(id+"F4.imprint","IMPRINT",EDGE,{"derivedFrom":sQuery(id+"F4.wireOp",EDGE,"E6.2.3.0")}),1.0]])]});
            var Q98;
            Q98=makeQuery(id+"F4.imprint","IMPRINT",FACE,{"disambiguationData":[TD([[makeQuery(id+"F4.imprint","IMPRINT",EDGE,{"derivedFrom":sQuery(id+"F4.wireOp",EDGE,"E6.1.0.0")}),1.0]])]});
            var Q99;
            Q99=makeQuery(id+"F4.imprint","IMPRINT",FACE,{"disambiguationData":[TD([[makeQuery(id+"F4.imprint","IMPRINT",EDGE,{"derivedFrom":sQuery(id+"F4.wireOp",EDGE,"E4")}),1.0]])]});
            extrude(context, id + "F5", {"entities" : qUnion([Q0, Q1, Q2, Q3, Q4, Q5, Q6, Q7, Q8, Q9, Q10, Q11, Q12, Q13, Q14, Q15, Q16, Q17, Q18, Q19, Q20, Q21, Q22, Q23, Q24, Q25, Q26, Q27, Q28, Q29, Q30, Q31, Q32, Q33, Q34, Q35, Q36, Q37, Q38, Q39, Q40, Q41, Q42, Q43, Q44, Q45, Q46, Q47, Q48, Q49, Q50, Q51, Q52, Q53, Q54, Q55, Q56, Q57, Q58, Q59, Q60, Q61, Q62, Q63, Q64, Q65, Q66, Q67, Q68, Q69, Q70, Q71, Q72, Q73, Q74, Q75, Q76, Q77, Q78, Q79, Q80, Q81, Q82, Q83, Q84, Q85, Q86, Q87, Q88, Q89, Q90, Q91, Q92, Q93, Q94, Q95, Q96, Q97, Q98, Q99]), "operationType" : NewBodyOperationType.REMOVE, "endBound" : BoundingType.THROUGH_ALL, "oppositeDirection" : true, "depth" : 25 * mm, "offsetDistance" : 25 * mm});
        }
        {
            var Q0;
            Q0=makeQuery(id+"F1.opExtrude","SWEPT_FACE",FACE,{"disambiguationData":[OSD([sQuery(id+"F0.wireOp",EDGE,"E0.top")])]});
            var sketch = newSketch(context, id + "F6", { "sketchPlane" : qUnion([Q0])});
            skText(sketch, "E7", { "text": "fill plate R1\n", "fontName": "OpenSans-Regular.ttf"});
            const initialGuessF6  = {"E7": [-0.08818, 0.00164, 1, 0, 0.0029]};
            skSetInitialGuess(sketch, initialGuessF6);
            skSolve(sketch);
        }
        {
            var Q0;
            Q0=qSketchRegion(id+"F6",true);
            extrude(context, id + "F7", {"entities" : qUnion([Q0]), "operationType" : NewBodyOperationType.REMOVE, "oppositeDirection" : true, "depth" : 2 * mm, "offsetDistance" : 25 * mm});
        }
        {
            var Q0;
            Q0=qCreatedBy(makeId("Top.planeOp"),FACE);
            var sketch = newSketch(context, id + "F8", { "sketchPlane" : qUnion([Q0])});
            skLineSegment(sketch, "E8.bottom", {"start": v(195.95, 87.88) * mm, "end": v(332.95, 87.88) * mm});
            skLineSegment(sketch, "E8.top", {"start": v(195.95, -52.12) * mm, "end": v(332.95, -52.12) * mm});
            skLineSegment(sketch, "E8.left", {"start": v(195.95, 87.88) * mm, "end": v(195.95, -52.12) * mm});
            skLineSegment(sketch, "E8.right", {"start": v(332.95, 87.88) * mm, "end": v(332.95, -52.12) * mm});
            skSolve(sketch);
        }
        {
            var Q0;
            Q0=qSketchRegion(id+"F8",true);
            extrude(context, id + "F9", {"entities" : qUnion([Q0]), "depth" : 50 * mm, "offsetDistance" : 25 * mm});
        }
        {
            var Q0;
            Q0=makeQuery(id+"F9.opExtrude","CAP_FACE",FACE,{"disambiguationData":[OSD([sQuery(id+"F8.wireOp",EDGE,"E8.bottom"),sQuery(id+"F8.wireOp",EDGE,"E8.top"),sQuery(id+"F8.wireOp",EDGE,"E8.left"),sQuery(id+"F8.wireOp",EDGE,"E8.right")])],"isStart":false});
            var sketch = newSketch(context, id + "F10", { "sketchPlane" : qUnion([Q0])});
            skCircle(sketch, "E9", {"center": v(210.95, 72.88) * mm, "radius": 6 * mm});
            skCircle(sketch, "E10", {"center": v(222.95, 60.88) * mm, "radius": 6 * mm});
            skCircle(sketch, "E11.0.1.0", {"center": v(210.95, 48.88) * mm, "radius": 6 * mm});
            skCircle(sketch, "E11.0.1.1", {"center": v(222.95, 36.88) * mm, "radius": 6 * mm});
            skCircle(sketch, "E11.0.2.0", {"center": v(210.95, 24.88) * mm, "radius": 6 * mm});
            skCircle(sketch, "E11.0.2.1", {"center": v(222.95, 12.88) * mm, "radius": 6 * mm});
            skCircle(sketch, "E11.0.3.0", {"center": v(210.95, 0.88) * mm, "radius": 6 * mm});
            skCircle(sketch, "E11.0.3.1", {"center": v(222.95, -11.12) * mm, "radius": 6 * mm});
            skCircle(sketch, "E11.0.4.0", {"center": v(210.95, -23.12) * mm, "radius": 6 * mm});
            skCircle(sketch, "E11.0.4.1", {"center": v(222.95, -35.12) * mm, "radius": 6 * mm});
            skCircle(sketch, "E11.1.0.0", {"center": v(234.95, 72.88) * mm, "radius": 6 * mm});
            skCircle(sketch, "E11.1.0.1", {"center": v(246.95, 60.88) * mm, "radius": 6 * mm});
            skCircle(sketch, "E11.1.1.0", {"center": v(234.95, 48.88) * mm, "radius": 6 * mm});
            skCircle(sketch, "E11.1.1.1", {"center": v(246.95, 36.88) * mm, "radius": 6 * mm});
            skCircle(sketch, "E11.1.2.0", {"center": v(234.95, 24.88) * mm, "radius": 6 * mm});
            skCircle(sketch, "E11.1.2.1", {"center": v(246.95, 12.88) * mm, "radius": 6 * mm});
            skCircle(sketch, "E11.1.3.0", {"center": v(234.95, 0.88) * mm, "radius": 6 * mm});
            skCircle(sketch, "E11.1.3.1", {"center": v(246.95, -11.12) * mm, "radius": 6 * mm});
            skCircle(sketch, "E11.1.4.0", {"center": v(234.95, -23.12) * mm, "radius": 6 * mm});
            skCircle(sketch, "E11.1.4.1", {"center": v(246.95, -35.12) * mm, "radius": 6 * mm});
            skCircle(sketch, "E11.2.0.0", {"center": v(258.95, 72.88) * mm, "radius": 6 * mm});
            skCircle(sketch, "E11.2.0.1", {"center": v(270.95, 60.88) * mm, "radius": 6 * mm});
            skCircle(sketch, "E11.2.1.0", {"center": v(258.95, 48.88) * mm, "radius": 6 * mm});
            skCircle(sketch, "E11.2.1.1", {"center": v(270.95, 36.88) * mm, "radius": 6 * mm});
            skCircle(sketch, "E11.2.2.0", {"center": v(258.95, 24.88) * mm, "radius": 6 * mm});
            skCircle(sketch, "E11.2.2.1", {"center": v(270.95, 12.88) * mm, "radius": 6 * mm});
            skCircle(sketch, "E11.2.3.0", {"center": v(258.95, 0.88) * mm, "radius": 6 * mm});
            skCircle(sketch, "E11.2.3.1", {"center": v(270.95, -11.12) * mm, "radius": 6 * mm});
            skCircle(sketch, "E11.2.4.0", {"center": v(258.95, -23.12) * mm, "radius": 6 * mm});
            skCircle(sketch, "E11.2.4.1", {"center": v(270.95, -35.12) * mm, "radius": 6 * mm});
            skCircle(sketch, "E11.3.0.0", {"center": v(282.95, 72.88) * mm, "radius": 6 * mm});
            skCircle(sketch, "E11.3.0.1", {"center": v(294.95, 60.88) * mm, "radius": 6 * mm});
            skCircle(sketch, "E11.3.1.0", {"center": v(282.95, 48.88) * mm, "radius": 6 * mm});
            skCircle(sketch, "E11.3.1.1", {"center": v(294.95, 36.88) * mm, "radius": 6 * mm});
            skCircle(sketch, "E11.3.2.0", {"center": v(282.95, 24.88) * mm, "radius": 6 * mm});
            skCircle(sketch, "E11.3.2.1", {"center": v(294.95, 12.88) * mm, "radius": 6 * mm});
            skCircle(sketch, "E11.3.3.0", {"center": v(282.95, 0.88) * mm, "radius": 6 * mm});
            skCircle(sketch, "E11.3.3.1", {"center": v(294.95, -11.12) * mm, "radius": 6 * mm});
            skCircle(sketch, "E11.3.4.0", {"center": v(282.95, -23.12) * mm, "radius": 6 * mm});
            skCircle(sketch, "E11.3.4.1", {"center": v(294.95, -35.12) * mm, "radius": 6 * mm});
            skCircle(sketch, "E11.4.0.0", {"center": v(306.95, 72.88) * mm, "radius": 6 * mm});
            skCircle(sketch, "E11.4.0.1", {"center": v(318.95, 60.88) * mm, "radius": 6 * mm});
            skCircle(sketch, "E11.4.1.0", {"center": v(306.95, 48.88) * mm, "radius": 6 * mm});
            skCircle(sketch, "E11.4.1.1", {"center": v(318.95, 36.88) * mm, "radius": 6 * mm});
            skCircle(sketch, "E11.4.2.0", {"center": v(306.95, 24.88) * mm, "radius": 6 * mm});
            skCircle(sketch, "E11.4.2.1", {"center": v(318.95, 12.88) * mm, "radius": 6 * mm});
            skCircle(sketch, "E11.4.3.0", {"center": v(306.95, 0.88) * mm, "radius": 6 * mm});
            skCircle(sketch, "E11.4.3.1", {"center": v(318.95, -11.12) * mm, "radius": 6 * mm});
            skCircle(sketch, "E11.4.4.0", {"center": v(306.95, -23.12) * mm, "radius": 6 * mm});
            skCircle(sketch, "E11.4.4.1", {"center": v(318.95, -35.12) * mm, "radius": 6 * mm});
            skLineSegment(sketch, "E11.direction1", {"start": v(210.95, 72.88) * mm, "end": v(234.95, 72.88) * mm, "construction": true});
            skLineSegment(sketch, "E11.direction2", {"start": v(210.95, 72.88) * mm, "end": v(210.95, 48.88) * mm, "construction": true});
            skSolve(sketch);
        }
        {
            var Q0;
            Q0=makeQuery(id+"F10.imprint","IMPRINT",FACE,{"disambiguationData":[TD([[makeQuery(id+"F10.imprint","IMPRINT",EDGE,{"derivedFrom":sQuery(id+"F10.wireOp",EDGE,"E9")}),1.0]])]});
            var Q1;
            Q1=makeQuery(id+"F10.imprint","IMPRINT",FACE,{"disambiguationData":[TD([[makeQuery(id+"F10.imprint","IMPRINT",EDGE,{"derivedFrom":sQuery(id+"F10.wireOp",EDGE,"E10")}),1.0]])]});
            var Q2;
            Q2=makeQuery(id+"F10.imprint","IMPRINT",FACE,{"disambiguationData":[TD([[makeQuery(id+"F10.imprint","IMPRINT",EDGE,{"derivedFrom":sQuery(id+"F10.wireOp",EDGE,"E11.0.1.0")}),1.0]])]});
            var Q3;
            Q3=makeQuery(id+"F10.imprint","IMPRINT",FACE,{"disambiguationData":[TD([[makeQuery(id+"F10.imprint","IMPRINT",EDGE,{"derivedFrom":sQuery(id+"F10.wireOp",EDGE,"E11.0.1.1")}),1.0]])]});
            var Q4;
            Q4=makeQuery(id+"F10.imprint","IMPRINT",FACE,{"disambiguationData":[TD([[makeQuery(id+"F10.imprint","IMPRINT",EDGE,{"derivedFrom":sQuery(id+"F10.wireOp",EDGE,"E11.0.2.0")}),1.0]])]});
            var Q5;
            Q5=makeQuery(id+"F10.imprint","IMPRINT",FACE,{"disambiguationData":[TD([[makeQuery(id+"F10.imprint","IMPRINT",EDGE,{"derivedFrom":sQuery(id+"F10.wireOp",EDGE,"E11.2.4.1")}),1.0]])]});
            var Q6;
            Q6=makeQuery(id+"F10.imprint","IMPRINT",FACE,{"disambiguationData":[TD([[makeQuery(id+"F10.imprint","IMPRINT",EDGE,{"derivedFrom":sQuery(id+"F10.wireOp",EDGE,"E11.3.0.0")}),1.0]])]});
            var Q7;
            Q7=makeQuery(id+"F10.imprint","IMPRINT",FACE,{"disambiguationData":[TD([[makeQuery(id+"F10.imprint","IMPRINT",EDGE,{"derivedFrom":sQuery(id+"F10.wireOp",EDGE,"E11.3.0.1")}),1.0]])]});
            var Q8;
            Q8=makeQuery(id+"F10.imprint","IMPRINT",FACE,{"disambiguationData":[TD([[makeQuery(id+"F10.imprint","IMPRINT",EDGE,{"derivedFrom":sQuery(id+"F10.wireOp",EDGE,"E11.3.1.0")}),1.0]])]});
            var Q9;
            Q9=makeQuery(id+"F10.imprint","IMPRINT",FACE,{"disambiguationData":[TD([[makeQuery(id+"F10.imprint","IMPRINT",EDGE,{"derivedFrom":sQuery(id+"F10.wireOp",EDGE,"E11.3.1.1")}),1.0]])]});
            var Q10;
            Q10=makeQuery(id+"F10.imprint","IMPRINT",FACE,{"disambiguationData":[TD([[makeQuery(id+"F10.imprint","IMPRINT",EDGE,{"derivedFrom":sQuery(id+"F10.wireOp",EDGE,"E11.3.2.0")}),1.0]])]});
            var Q11;
            Q11=makeQuery(id+"F10.imprint","IMPRINT",FACE,{"disambiguationData":[TD([[makeQuery(id+"F10.imprint","IMPRINT",EDGE,{"derivedFrom":sQuery(id+"F10.wireOp",EDGE,"E11.3.2.1")}),1.0]])]});
            var Q12;
            Q12=makeQuery(id+"F10.imprint","IMPRINT",FACE,{"disambiguationData":[TD([[makeQuery(id+"F10.imprint","IMPRINT",EDGE,{"derivedFrom":sQuery(id+"F10.wireOp",EDGE,"E11.3.3.0")}),1.0]])]});
            var Q13;
            Q13=makeQuery(id+"F10.imprint","IMPRINT",FACE,{"disambiguationData":[TD([[makeQuery(id+"F10.imprint","IMPRINT",EDGE,{"derivedFrom":sQuery(id+"F10.wireOp",EDGE,"E11.3.3.1")}),1.0]])]});
            var Q14;
            Q14=makeQuery(id+"F10.imprint","IMPRINT",FACE,{"disambiguationData":[TD([[makeQuery(id+"F10.imprint","IMPRINT",EDGE,{"derivedFrom":sQuery(id+"F10.wireOp",EDGE,"E11.3.4.0")}),1.0]])]});
            var Q15;
            Q15=makeQuery(id+"F10.imprint","IMPRINT",FACE,{"disambiguationData":[TD([[makeQuery(id+"F10.imprint","IMPRINT",EDGE,{"derivedFrom":sQuery(id+"F10.wireOp",EDGE,"E11.3.4.1")}),1.0]])]});
            var Q16;
            Q16=makeQuery(id+"F10.imprint","IMPRINT",FACE,{"disambiguationData":[TD([[makeQuery(id+"F10.imprint","IMPRINT",EDGE,{"derivedFrom":sQuery(id+"F10.wireOp",EDGE,"E11.4.0.0")}),1.0]])]});
            var Q17;
            Q17=makeQuery(id+"F10.imprint","IMPRINT",FACE,{"disambiguationData":[TD([[makeQuery(id+"F10.imprint","IMPRINT",EDGE,{"derivedFrom":sQuery(id+"F10.wireOp",EDGE,"E11.4.3.1")}),1.0]])]});
            var Q18;
            Q18=makeQuery(id+"F10.imprint","IMPRINT",FACE,{"disambiguationData":[TD([[makeQuery(id+"F10.imprint","IMPRINT",EDGE,{"derivedFrom":sQuery(id+"F10.wireOp",EDGE,"E11.4.4.0")}),1.0]])]});
            var Q19;
            Q19=makeQuery(id+"F10.imprint","IMPRINT",FACE,{"disambiguationData":[TD([[makeQuery(id+"F10.imprint","IMPRINT",EDGE,{"derivedFrom":sQuery(id+"F10.wireOp",EDGE,"E11.4.4.1")}),1.0]])]});
            var Q20;
            Q20=makeQuery(id+"F10.imprint","IMPRINT",FACE,{"disambiguationData":[TD([[makeQuery(id+"F10.imprint","IMPRINT",EDGE,{"derivedFrom":sQuery(id+"F10.wireOp",EDGE,"E11.4.3.0")}),1.0]])]});
            var Q21;
            Q21=makeQuery(id+"F10.imprint","IMPRINT",FACE,{"disambiguationData":[TD([[makeQuery(id+"F10.imprint","IMPRINT",EDGE,{"derivedFrom":sQuery(id+"F10.wireOp",EDGE,"E11.4.2.1")}),1.0]])]});
            var Q22;
            Q22=makeQuery(id+"F10.imprint","IMPRINT",FACE,{"disambiguationData":[TD([[makeQuery(id+"F10.imprint","IMPRINT",EDGE,{"derivedFrom":sQuery(id+"F10.wireOp",EDGE,"E11.4.2.0")}),1.0]])]});
            var Q23;
            Q23=makeQuery(id+"F10.imprint","IMPRINT",FACE,{"disambiguationData":[TD([[makeQuery(id+"F10.imprint","IMPRINT",EDGE,{"derivedFrom":sQuery(id+"F10.wireOp",EDGE,"E11.4.1.1")}),1.0]])]});
            var Q24;
            Q24=makeQuery(id+"F10.imprint","IMPRINT",FACE,{"disambiguationData":[TD([[makeQuery(id+"F10.imprint","IMPRINT",EDGE,{"derivedFrom":sQuery(id+"F10.wireOp",EDGE,"E11.4.1.0")}),1.0]])]});
            var Q25;
            Q25=makeQuery(id+"F10.imprint","IMPRINT",FACE,{"disambiguationData":[TD([[makeQuery(id+"F10.imprint","IMPRINT",EDGE,{"derivedFrom":sQuery(id+"F10.wireOp",EDGE,"E11.4.0.1")}),1.0]])]});
            var Q26;
            Q26=makeQuery(id+"F10.imprint","IMPRINT",FACE,{"disambiguationData":[TD([[makeQuery(id+"F10.imprint","IMPRINT",EDGE,{"derivedFrom":sQuery(id+"F10.wireOp",EDGE,"E11.2.4.0")}),1.0]])]});
            var Q27;
            Q27=makeQuery(id+"F10.imprint","IMPRINT",FACE,{"disambiguationData":[TD([[makeQuery(id+"F10.imprint","IMPRINT",EDGE,{"derivedFrom":sQuery(id+"F10.wireOp",EDGE,"E11.2.3.1")}),1.0]])]});
            var Q28;
            Q28=makeQuery(id+"F10.imprint","IMPRINT",FACE,{"disambiguationData":[TD([[makeQuery(id+"F10.imprint","IMPRINT",EDGE,{"derivedFrom":sQuery(id+"F10.wireOp",EDGE,"E11.2.3.0")}),1.0]])]});
            var Q29;
            Q29=makeQuery(id+"F10.imprint","IMPRINT",FACE,{"disambiguationData":[TD([[makeQuery(id+"F10.imprint","IMPRINT",EDGE,{"derivedFrom":sQuery(id+"F10.wireOp",EDGE,"E11.2.2.1")}),1.0]])]});
            var Q30;
            Q30=makeQuery(id+"F10.imprint","IMPRINT",FACE,{"disambiguationData":[TD([[makeQuery(id+"F10.imprint","IMPRINT",EDGE,{"derivedFrom":sQuery(id+"F10.wireOp",EDGE,"E11.2.2.0")}),1.0]])]});
            var Q31;
            Q31=makeQuery(id+"F10.imprint","IMPRINT",FACE,{"disambiguationData":[TD([[makeQuery(id+"F10.imprint","IMPRINT",EDGE,{"derivedFrom":sQuery(id+"F10.wireOp",EDGE,"E11.2.1.1")}),1.0]])]});
            var Q32;
            Q32=makeQuery(id+"F10.imprint","IMPRINT",FACE,{"disambiguationData":[TD([[makeQuery(id+"F10.imprint","IMPRINT",EDGE,{"derivedFrom":sQuery(id+"F10.wireOp",EDGE,"E11.2.1.0")}),1.0]])]});
            var Q33;
            Q33=makeQuery(id+"F10.imprint","IMPRINT",FACE,{"disambiguationData":[TD([[makeQuery(id+"F10.imprint","IMPRINT",EDGE,{"derivedFrom":sQuery(id+"F10.wireOp",EDGE,"E11.2.0.1")}),1.0]])]});
            var Q34;
            Q34=makeQuery(id+"F10.imprint","IMPRINT",FACE,{"disambiguationData":[TD([[makeQuery(id+"F10.imprint","IMPRINT",EDGE,{"derivedFrom":sQuery(id+"F10.wireOp",EDGE,"E11.2.0.0")}),1.0]])]});
            var Q35;
            Q35=makeQuery(id+"F10.imprint","IMPRINT",FACE,{"disambiguationData":[TD([[makeQuery(id+"F10.imprint","IMPRINT",EDGE,{"derivedFrom":sQuery(id+"F10.wireOp",EDGE,"E11.1.4.1")}),1.0]])]});
            var Q36;
            Q36=makeQuery(id+"F10.imprint","IMPRINT",FACE,{"disambiguationData":[TD([[makeQuery(id+"F10.imprint","IMPRINT",EDGE,{"derivedFrom":sQuery(id+"F10.wireOp",EDGE,"E11.1.4.0")}),1.0]])]});
            var Q37;
            Q37=makeQuery(id+"F10.imprint","IMPRINT",FACE,{"disambiguationData":[TD([[makeQuery(id+"F10.imprint","IMPRINT",EDGE,{"derivedFrom":sQuery(id+"F10.wireOp",EDGE,"E11.1.3.1")}),1.0]])]});
            var Q38;
            Q38=makeQuery(id+"F10.imprint","IMPRINT",FACE,{"disambiguationData":[TD([[makeQuery(id+"F10.imprint","IMPRINT",EDGE,{"derivedFrom":sQuery(id+"F10.wireOp",EDGE,"E11.1.3.0")}),1.0]])]});
            var Q39;
            Q39=makeQuery(id+"F10.imprint","IMPRINT",FACE,{"disambiguationData":[TD([[makeQuery(id+"F10.imprint","IMPRINT",EDGE,{"derivedFrom":sQuery(id+"F10.wireOp",EDGE,"E11.1.2.1")}),1.0]])]});
            var Q40;
            Q40=makeQuery(id+"F10.imprint","IMPRINT",FACE,{"disambiguationData":[TD([[makeQuery(id+"F10.imprint","IMPRINT",EDGE,{"derivedFrom":sQuery(id+"F10.wireOp",EDGE,"E11.1.2.0")}),1.0]])]});
            var Q41;
            Q41=makeQuery(id+"F10.imprint","IMPRINT",FACE,{"disambiguationData":[TD([[makeQuery(id+"F10.imprint","IMPRINT",EDGE,{"derivedFrom":sQuery(id+"F10.wireOp",EDGE,"E11.1.1.1")}),1.0]])]});
            var Q42;
            Q42=makeQuery(id+"F10.imprint","IMPRINT",FACE,{"disambiguationData":[TD([[makeQuery(id+"F10.imprint","IMPRINT",EDGE,{"derivedFrom":sQuery(id+"F10.wireOp",EDGE,"E11.1.1.0")}),1.0]])]});
            var Q43;
            Q43=makeQuery(id+"F10.imprint","IMPRINT",FACE,{"disambiguationData":[TD([[makeQuery(id+"F10.imprint","IMPRINT",EDGE,{"derivedFrom":sQuery(id+"F10.wireOp",EDGE,"E11.1.0.1")}),1.0]])]});
            var Q44;
            Q44=makeQuery(id+"F10.imprint","IMPRINT",FACE,{"disambiguationData":[TD([[makeQuery(id+"F10.imprint","IMPRINT",EDGE,{"derivedFrom":sQuery(id+"F10.wireOp",EDGE,"E11.1.0.0")}),1.0]])]});
            var Q45;
            Q45=makeQuery(id+"F10.imprint","IMPRINT",FACE,{"disambiguationData":[TD([[makeQuery(id+"F10.imprint","IMPRINT",EDGE,{"derivedFrom":sQuery(id+"F10.wireOp",EDGE,"E11.0.4.1")}),1.0]])]});
            var Q46;
            Q46=makeQuery(id+"F10.imprint","IMPRINT",FACE,{"disambiguationData":[TD([[makeQuery(id+"F10.imprint","IMPRINT",EDGE,{"derivedFrom":sQuery(id+"F10.wireOp",EDGE,"E11.0.4.0")}),1.0]])]});
            var Q47;
            Q47=makeQuery(id+"F10.imprint","IMPRINT",FACE,{"disambiguationData":[TD([[makeQuery(id+"F10.imprint","IMPRINT",EDGE,{"derivedFrom":sQuery(id+"F10.wireOp",EDGE,"E11.0.3.1")}),1.0]])]});
            var Q48;
            Q48=makeQuery(id+"F10.imprint","IMPRINT",FACE,{"disambiguationData":[TD([[makeQuery(id+"F10.imprint","IMPRINT",EDGE,{"derivedFrom":sQuery(id+"F10.wireOp",EDGE,"E11.0.3.0")}),1.0]])]});
            var Q49;
            Q49=makeQuery(id+"F10.imprint","IMPRINT",FACE,{"disambiguationData":[TD([[makeQuery(id+"F10.imprint","IMPRINT",EDGE,{"derivedFrom":sQuery(id+"F10.wireOp",EDGE,"E11.0.2.1")}),1.0]])]});
            extrude(context, id + "F11", {"entities" : qUnion([Q0, Q1, Q2, Q3, Q4, Q5, Q6, Q7, Q8, Q9, Q10, Q11, Q12, Q13, Q14, Q15, Q16, Q17, Q18, Q19, Q20, Q21, Q22, Q23, Q24, Q25, Q26, Q27, Q28, Q29, Q30, Q31, Q32, Q33, Q34, Q35, Q36, Q37, Q38, Q39, Q40, Q41, Q42, Q43, Q44, Q45, Q46, Q47, Q48, Q49]), "operationType" : NewBodyOperationType.REMOVE, "endBound" : BoundingType.THROUGH_ALL, "oppositeDirection" : true, "depth" : 25 * mm, "offsetDistance" : 25 * mm});
        }
        {
            var Q0;
            Q0=makeQuery(id+"F9.opExtrude","SWEPT_FACE",FACE,{"disambiguationData":[OSD([sQuery(id+"F8.wireOp",EDGE,"E8.top")])]});
            var sketch = newSketch(context, id + "F12", { "sketchPlane" : qUnion([Q0])});
            skText(sketch, "E12", { "text": "charge block R1", "fontName": "OpenSans-Regular.ttf"});
            const initialGuessF12  = {"E12": [0.21183, 0.02567, 1, 0, 0.01094]};
            skSetInitialGuess(sketch, initialGuessF12);
            skSolve(sketch);
        }
        {
            var Q0;
            Q0=qSketchRegion(id+"F12",true);
            extrude(context, id + "F13", {"entities" : qUnion([Q0]), "operationType" : NewBodyOperationType.REMOVE, "oppositeDirection" : true, "depth" : 2 * mm, "offsetDistance" : 25 * mm});
        }
        {
            var Q0;
            Q0=makeQuery(id+"F1.opExtrude","CAP_FACE",FACE,{"disambiguationData":[OSD([sQuery(id+"F0.wireOp",EDGE,"E0.bottom"),sQuery(id+"F0.wireOp",EDGE,"E0.top"),sQuery(id+"F0.wireOp",EDGE,"E0.left"),sQuery(id+"F0.wireOp",EDGE,"E0.right")])],"isStart":false});
            var sketch = newSketch(context, id + "F14", { "sketchPlane" : qUnion([Q0])});
            skLineSegment(sketch, "E13.0", {"start": v(-132.2, 107.86) * mm, "end": v(-132.2, -52.14) * mm});
            skLineSegment(sketch, "E14.0.1", {"start": v(-132.2, -52.14) * mm, "end": v(14.8, -52.14) * mm});
            skLineSegment(sketch, "E14.0.3", {"start": v(14.8, 107.86) * mm, "end": v(-132.2, 107.86) * mm});
            skLineSegment(sketch, "E15.0", {"start": v(9.8, 102.86) * mm, "end": v(-127.2, 102.86) * mm});
            skLineSegment(sketch, "E15.2", {"start": v(-127.2, -47.14) * mm, "end": v(9.8, -47.14) * mm});
            skLineSegment(sketch, "E15.3", {"start": v(-127.2, 102.86) * mm, "end": v(-127.2, -47.14) * mm});
            skLineSegment(sketch, "E16.0", {"start": v(14.8, 107.86) * mm, "end": v(14.8, -52.14) * mm});
            skLineSegment(sketch, "E17", {"start": v(9.8, 102.86) * mm, "end": v(9.8, -47.14) * mm});
            skSolve(sketch);
        }
        {
            var Q0;
            {var subQ3=sQuery(id+"F14.wireOp",EDGE,"E13.0");Q0=makeQuery(id+"F14.imprint","IMPRINT",FACE,{"disambiguationData":[TD([[makeQuery(id+"F14.imprint","IMPRINT",EDGE,{"derivedFrom":subQ3}),1.0]])]});}
            var Q1;
            Q1=qConstructionFilter(qBodyType(qCreatedBy(id+"F14",EDGE),BodyType.WIRE),ConstructionObject.NO);
            extrude(context, id + "F15", {"entities" : qUnion([Q0]), "operationType" : NewBodyOperationType.ADD, "surfaceEntities" : qUnion([Q1]), "depth" : 5 * mm, "offsetDistance" : 25 * mm});
        }
    });
